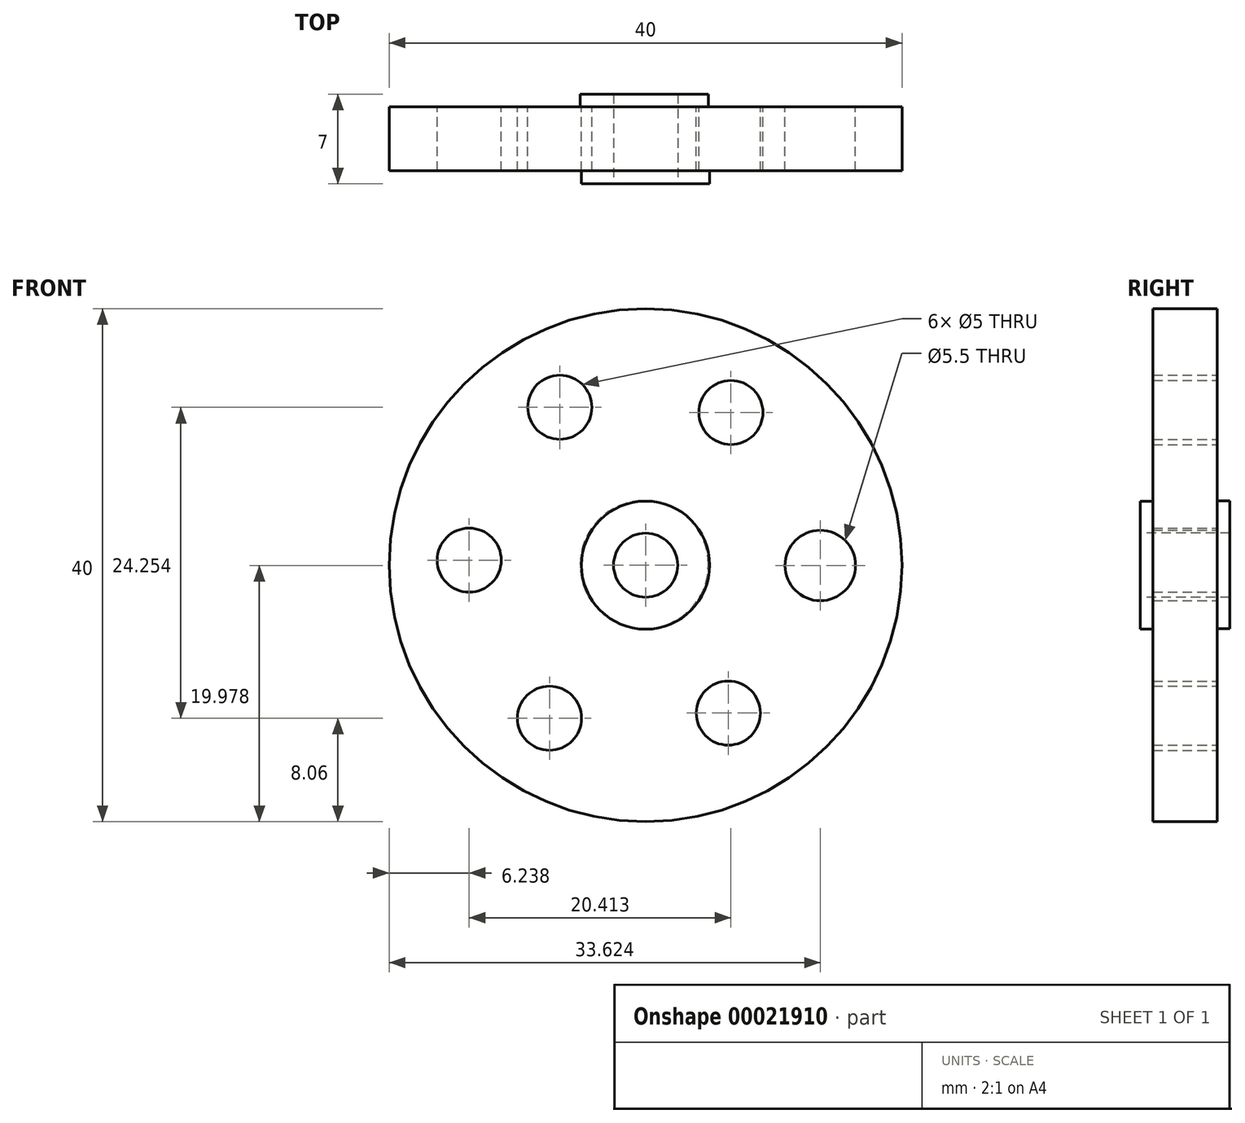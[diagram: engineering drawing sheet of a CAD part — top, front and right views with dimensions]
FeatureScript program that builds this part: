
annotation { "Feature Type Name" : "Feature", "Feature Type Description" : "" }
export const myFeature = defineFeature(function(context is Context, id is Id, definition is map)
    precondition{}
    {
        {
            var Q0;
            Q0=qCreatedBy(makeId("Front.planeOp"),FACE);
            var sketch = newSketch(context, id + "F0", { "sketchPlane" : qUnion([Q0])});
            skCircle(sketch, "E0", {"center": v(-6.06, 1.24) * mm, "radius": 20 * mm});
            skSolve(sketch);
        }
        {
            var Q0;
            Q0=makeQuery(id+"F0.imprint","IMPRINT",FACE,{"disambiguationData":[TD([[makeQuery(id+"F0.imprint","IMPRINT",EDGE,{"derivedFrom":sQuery(id+"F0.wireOp",EDGE,"E0")}),1.0]])]});
            var sketch = newSketch(context, id + "F1", { "sketchPlane" : qUnion([Q0])});
            skCircle(sketch, "E1.cCircle", {"center": v(-6.13, 1.23) * mm, "radius": 9.91 * mm, "construction": true});
            skLineSegment(sketch, "E1.0", {"start": v(-17.57, 1.4) * mm, "end": v(-11.7, 11.23) * mm});
            skLineSegment(sketch, "E1.1", {"start": v(-11.7, 11.23) * mm, "end": v(-0.25, 11.06) * mm});
            skLineSegment(sketch, "E1.2", {"start": v(-0.25, 11.06) * mm, "end": v(5.32, 1.06) * mm});
            skLineSegment(sketch, "E1.3", {"start": v(5.32, 1.06) * mm, "end": v(-0.55, -8.77) * mm});
            skLineSegment(sketch, "E1.4", {"start": v(-0.55, -8.77) * mm, "end": v(-12, -8.6) * mm});
            skLineSegment(sketch, "E1.5", {"start": v(-12, -8.6) * mm, "end": v(-17.57, 1.4) * mm});
            skSolve(sketch);
        }
        {
            var Q0;
            Q0=makeQuery(id+"F0.imprint","IMPRINT",FACE,{"disambiguationData":[TD([[makeQuery(id+"F0.imprint","IMPRINT",EDGE,{"derivedFrom":sQuery(id+"F0.wireOp",EDGE,"E0")}),1.0]])]});
            var sketch = newSketch(context, id + "F2", { "sketchPlane" : qUnion([Q0])});
            skCircle(sketch, "E2", {"center": v(-19.82, 1.63) * mm, "radius": 2.5 * mm});
            skCircle(sketch, "E3", {"center": v(-12.75, 13.55) * mm, "radius": 2.5 * mm});
            skCircle(sketch, "E4", {"center": v(0.6, 13.15) * mm, "radius": 2.5 * mm});
            skCircle(sketch, "E5", {"center": v(7.56, 1.22) * mm, "radius": 2.75 * mm});
            skCircle(sketch, "E6", {"center": v(-13.56, -10.7) * mm, "radius": 2.5 * mm});
            skCircle(sketch, "E7", {"center": v(0.39, -10.3) * mm, "radius": 2.5 * mm});
            skSolve(sketch);
        }
        {
            var Q0;
            Q0 = qSketchRegion(id + "F0", true);
            extrude(context, id + "F3", {"entities" : qUnion([Q0]), "depth" : 5 * mm});
        }
        {
            var Q0;
            Q0 = qSketchRegion(id + "F2", true);
            extrude(context, id + "F4", {"entities" : qUnion([Q0]), "operationType" : NewBodyOperationType.REMOVE, "endBound" : BoundingType.THROUGH_ALL, "depth" : 25.4 * mm});
        }
        {
            var Q0;
            Q0=makeQuery(id+"F3.opExtrude","CAP_FACE",FACE,{"disambiguationData":[OSD([sQuery(id+"F0.wireOp",EDGE,"E0")])],"isStart":false});
            var sketch = newSketch(context, id + "F5", { "sketchPlane" : qUnion([Q0])});
            skCircle(sketch, "E8", {"center": v(-6.06, 1.24) * mm, "radius": 5 * mm});
            skSolve(sketch);
        }
        {
            var Q0;
            Q0 = qSketchRegion(id + "F5", true);
            extrude(context, id + "F6", {"entities" : qUnion([Q0]), "operationType" : NewBodyOperationType.ADD, "depth" : 1 * mm});
        }
        {
            var Q0;
            Q0=makeQuery(id+"F1.imprint","IMPRINT",FACE,{"disambiguationData":[TD([[makeQuery(id+"F1.imprint","IMPRINT",EDGE,{"derivedFrom":sQuery(id+"F1.wireOp",EDGE,"E1.0")}),-1.0]])]});
            var sketch = newSketch(context, id + "F7", { "sketchPlane" : qUnion([Q0])});
            skCircle(sketch, "E9", {"center": v(-6.17, 1.27) * mm, "radius": 5 * mm});
            skSolve(sketch);
        }
        {
            var Q0;
            Q0 = qSketchRegion(id + "F7", true);
            extrude(context, id + "F8", {"entities" : qUnion([Q0]), "operationType" : NewBodyOperationType.ADD, "oppositeDirection" : true, "depth" : 1 * mm});
        }
        {
            var Q0;
            Q0=makeQuery(id+"F6.opExtrude","CAP_FACE",FACE,{"disambiguationData":[OSD([sQuery(id+"F5.wireOp",EDGE,"E8")])],"isStart":false});
            var sketch = newSketch(context, id + "F9", { "sketchPlane" : qUnion([Q0])});
            skCircle(sketch, "E10", {"center": v(-6.06, 1.24) * mm, "radius": 2.5 * mm});
            skSolve(sketch);
        }
        {
            var Q0;
            Q0 = qSketchRegion(id + "F9", true);
            extrude(context, id + "F10", {"entities" : qUnion([Q0]), "operationType" : NewBodyOperationType.REMOVE, "endBound" : BoundingType.THROUGH_ALL, "oppositeDirection" : true, "depth" : 25.4 * mm});
        }
    });
